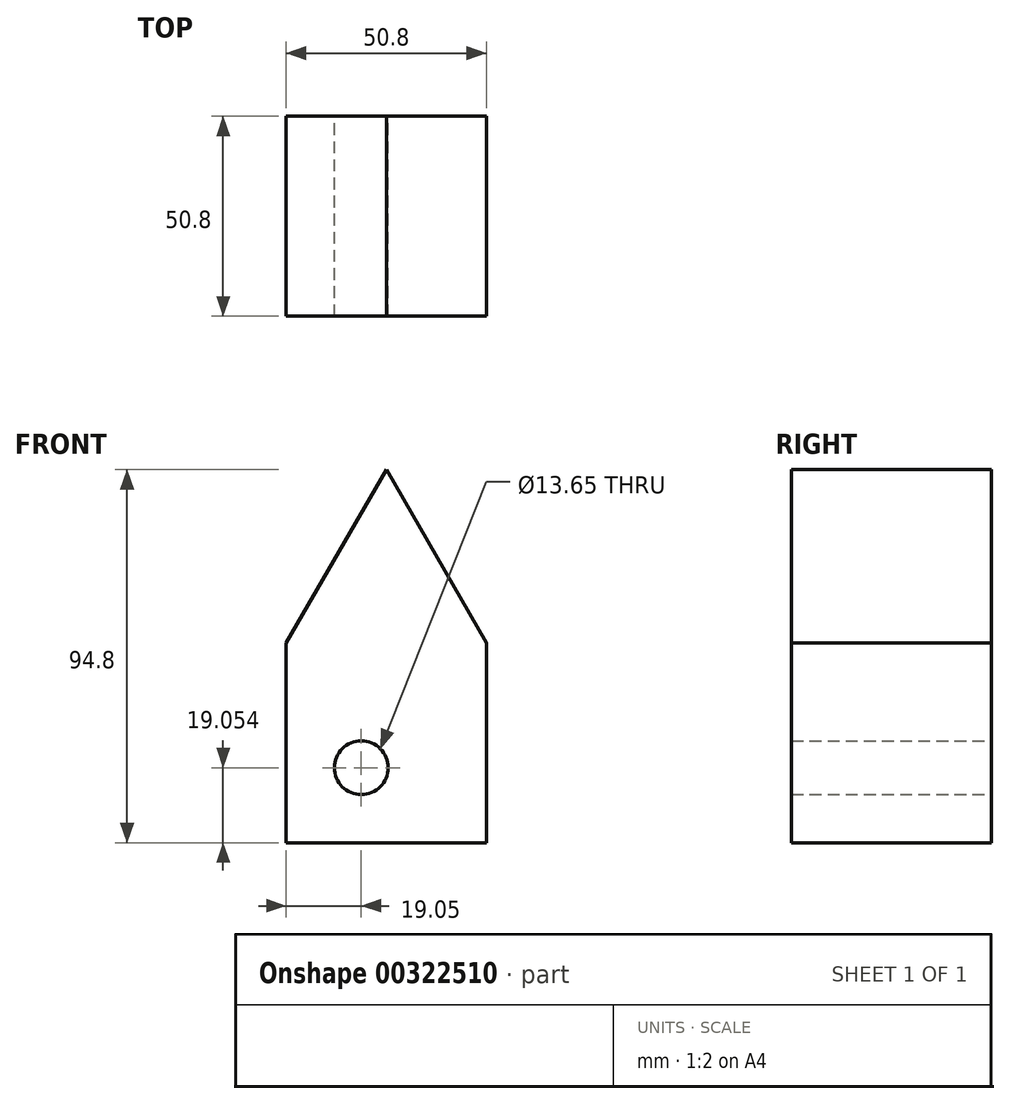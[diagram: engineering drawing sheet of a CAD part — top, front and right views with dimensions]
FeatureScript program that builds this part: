
annotation { "Feature Type Name" : "Feature", "Feature Type Description" : "" }
export const myFeature = defineFeature(function(context is Context, id is Id, definition is map)
    precondition{}
    {
        {
            var Q0;
            Q0=qCreatedBy(makeId("Front.planeOp"),FACE);
            var sketch = newSketch(context, id + "F0", { "sketchPlane" : qUnion([Q0])});
            skLineSegment(sketch, "E0.bottom", {"start": v(-25.4, 3.67) * mm, "end": v(25.4, 3.67) * mm});
            skLineSegment(sketch, "E0.top", {"start": v(-25.4, -47.13) * mm, "end": v(25.4, -47.13) * mm});
            skLineSegment(sketch, "E0.left", {"start": v(-25.4, 3.67) * mm, "end": v(-25.4, -47.13) * mm});
            skLineSegment(sketch, "E0.right", {"start": v(25.4, 3.67) * mm, "end": v(25.4, -47.13) * mm});
            skLineSegment(sketch, "E1", {"start": v(-25.4, 3.67) * mm, "end": v(0, 47.67) * mm});
            skLineSegment(sketch, "E2", {"start": v(25.4, 3.67) * mm, "end": v(0, 47.67) * mm});
            skLineSegment(sketch, "E3.0", {"start": v(-25.4, -28.08) * mm, "end": v(25.4, -28.08) * mm});
            skLineSegment(sketch, "E4.0", {"start": v(-6.35, 3.67) * mm, "end": v(-6.35, -47.13) * mm});
            skCircle(sketch, "E5", {"center": v(-6.35, -28.08) * mm, "radius": 6.82 * mm});
            skPoint(sketch, "E5.centerSnap0", {"position": v(-6.35, -21.73) * mm});
            skSolve(sketch);
        }
        {
            var Q0;
            Q0 = qSketchRegion(id + "F0", true);
            extrude(context, id + "F1", {"entities" : qUnion([Q0]), "depth" : 50.8 * mm});
        }
    });
